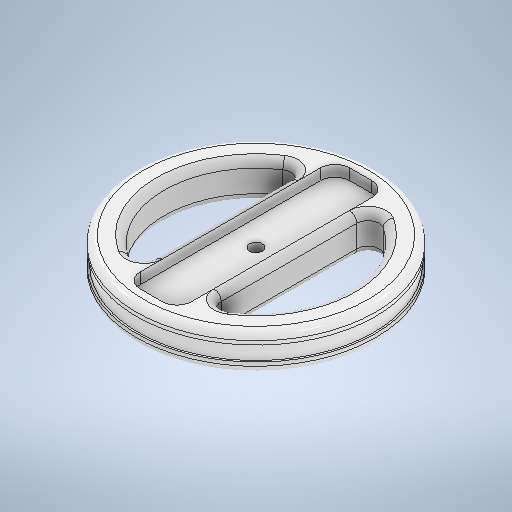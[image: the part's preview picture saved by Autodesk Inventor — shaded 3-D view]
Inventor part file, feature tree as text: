
AUTODESK INVENTOR PART (.ipt)
format: ipt  version: 2025 (Build 290162000, 162)  size: 623,104 bytes
history: native  units: mm
features: fillet x4, sketch x4, extrude x3, other x1
ambient origin geometry x8: Origin, YZ Plane, XZ Plane, XY Plane, X Axis, Y Axis, Z Axis, Center Point
bodies: Solide1 (feature_tree)
feature tree (12):
  other  "Révolution1"
  extrude  "Extrusion1"  Depth=32.5mm
  fillet  "Congé1"  Radius=10.0mm
  extrude  "Extrusion2"  Depth=3.0mm
  fillet  "Congé2"  Radius=0.5mm
  extrude  "Extrusion3"  TaperAngle=90.0deg  [1 undecoded]
  fillet  "Congé3"  Radius=14.0mm
  fillet  "Congé4"  Radius=57.0mm
  sketch  "Esquisse2"
  sketch  "Esquisse3"
  sketch  "Esquisse4"
  sketch  "Esquisse5"
note: 1 required parameter value undecoded (feature->parameter linkage not recoverable at this tier; creation-order binding heuristic only, values carry confidence <= 0.55)
